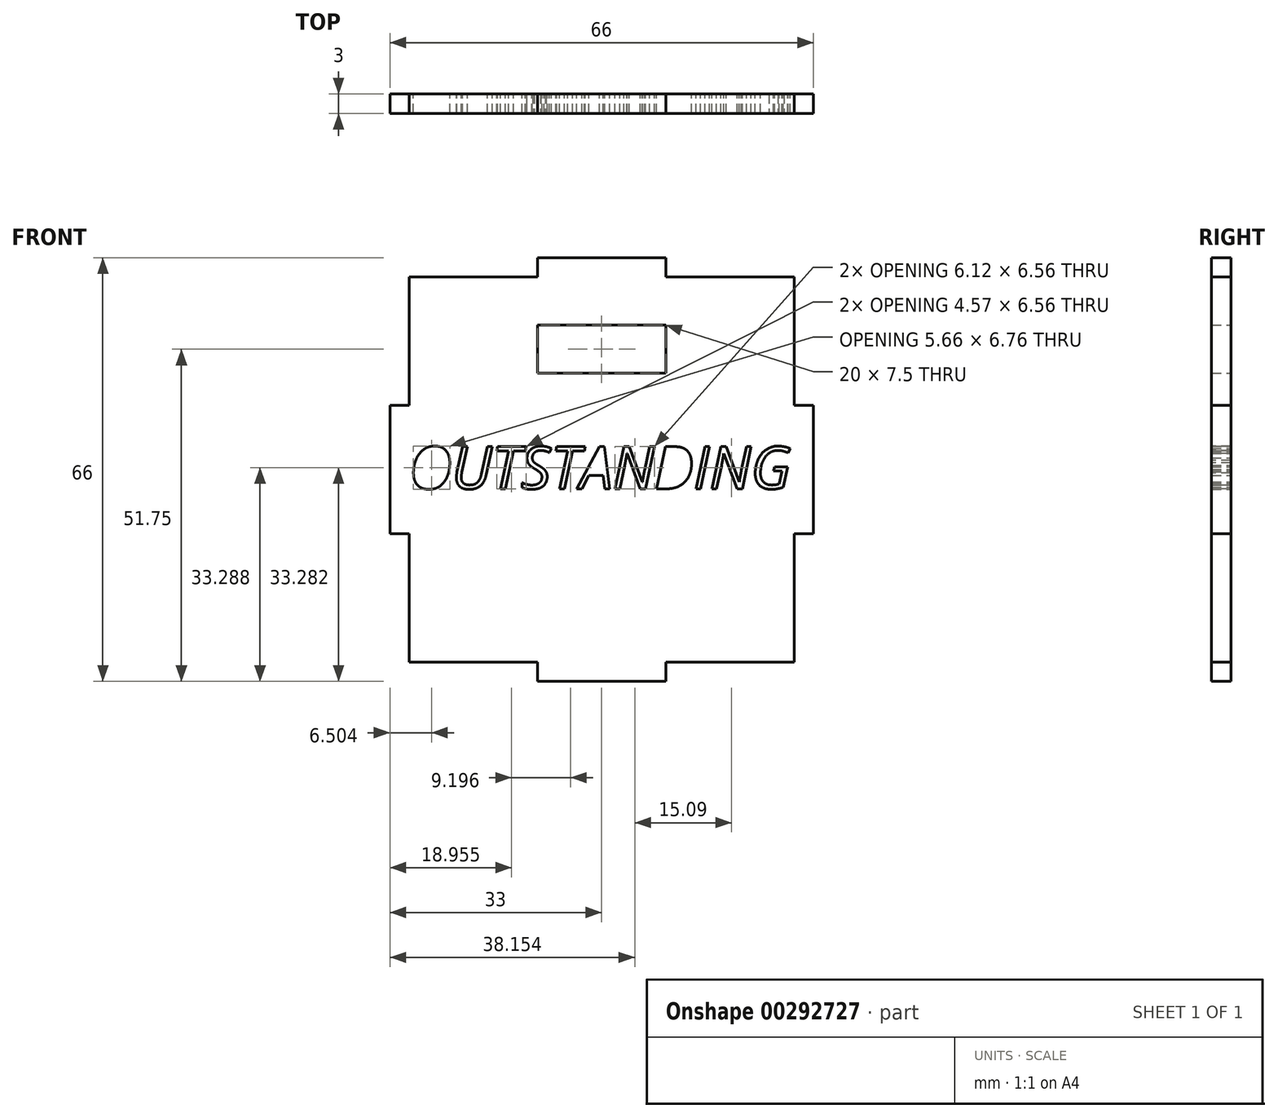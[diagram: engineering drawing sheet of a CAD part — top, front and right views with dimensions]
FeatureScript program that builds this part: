
annotation { "Feature Type Name" : "Feature", "Feature Type Description" : "" }
export const myFeature = defineFeature(function(context is Context, id is Id, definition is map)
    precondition{}
    {
        {
            var Q0;
            Q0=qCreatedBy(makeId("Front.planeOp"),FACE);
            var sketch = newSketch(context, id + "F0", { "sketchPlane" : qUnion([Q0])});
            skLineSegment(sketch, "E0", {"start": v(-33, 0) * mm, "end": v(-33, 10) * mm});
            skLineSegment(sketch, "E1", {"start": v(-33, 10) * mm, "end": v(-30, 10) * mm});
            skLineSegment(sketch, "E2", {"start": v(-30, 10) * mm, "end": v(-30, 30) * mm});
            skLineSegment(sketch, "E3", {"start": v(-30, 30) * mm, "end": v(-10, 30) * mm});
            skLineSegment(sketch, "E4", {"start": v(-10, 30) * mm, "end": v(-10, 33) * mm});
            skLineSegment(sketch, "E5", {"start": v(-10, 33) * mm, "end": v(0, 33) * mm});
            skLineSegment(sketch, "E6", {"start": v(-33, 0) * mm, "end": v(0, 0) * mm, "construction": true});
            skLineSegment(sketch, "E7", {"start": v(0, 0) * mm, "end": v(0, 33) * mm, "construction": true});
            skLineSegment(sketch, "E8.MirrorCS", {"start": v(33, 10) * mm, "end": v(30, 10) * mm});
            skLineSegment(sketch, "E9.MirrorCS", {"start": v(30, 10) * mm, "end": v(30, 30) * mm});
            skLineSegment(sketch, "E10.MirrorCS", {"start": v(30, 30) * mm, "end": v(10, 30) * mm});
            skLineSegment(sketch, "E11.MirrorCS", {"start": v(10, 30) * mm, "end": v(10, 33) * mm});
            skLineSegment(sketch, "E12.MirrorCS", {"start": v(33, 0) * mm, "end": v(33, 10) * mm});
            skLineSegment(sketch, "E13.MirrorCS", {"start": v(10, 33) * mm, "end": v(0, 33) * mm});
            skLineSegment(sketch, "E14.MirrorCS", {"start": v(33, -10) * mm, "end": v(30, -10) * mm});
            skLineSegment(sketch, "E15.MirrorCS", {"start": v(-10, -33) * mm, "end": v(0, -33) * mm});
            skLineSegment(sketch, "E16.MirrorCS", {"start": v(-33, 0) * mm, "end": v(-33, -10) * mm});
            skLineSegment(sketch, "E17.MirrorCS", {"start": v(30, -30) * mm, "end": v(10, -30) * mm});
            skLineSegment(sketch, "E18.MirrorCS", {"start": v(-33, -10) * mm, "end": v(-30, -10) * mm});
            skLineSegment(sketch, "E19.MirrorCS", {"start": v(-30, -10) * mm, "end": v(-30, -30) * mm});
            skLineSegment(sketch, "E20.MirrorCS", {"start": v(30, -10) * mm, "end": v(30, -30) * mm});
            skLineSegment(sketch, "E21.MirrorCS", {"start": v(10, -30) * mm, "end": v(10, -33) * mm});
            skLineSegment(sketch, "E22.MirrorCS", {"start": v(10, -33) * mm, "end": v(0, -33) * mm});
            skLineSegment(sketch, "E23.MirrorCS", {"start": v(-10, -30) * mm, "end": v(-10, -33) * mm});
            skLineSegment(sketch, "E24.MirrorCS", {"start": v(33, 0) * mm, "end": v(33, -10) * mm});
            skLineSegment(sketch, "E25.MirrorCS", {"start": v(-30, -30) * mm, "end": v(-10, -30) * mm});
            skLineSegment(sketch, "E26.bottom", {"start": v(10, 15) * mm, "end": v(-10, 15) * mm});
            skLineSegment(sketch, "E26.top", {"start": v(10, 22.5) * mm, "end": v(-10, 22.5) * mm});
            skLineSegment(sketch, "E26.left", {"start": v(10, 15) * mm, "end": v(10, 22.5) * mm});
            skLineSegment(sketch, "E26.right", {"start": v(-10, 15) * mm, "end": v(-10, 22.5) * mm});
            skPoint(sketch, "E26.middle", {"position": v(0, 18.75) * mm});
            skText(sketch, "E27", { "text": "OUTSTANDING", "fontName": "OpenSans-Italic.ttf"});
            const initialGuessF0  = {"E27": [-0.03, -0.003, 1, 0, 0.00662]};
            skSetInitialGuess(sketch, initialGuessF0);
            skSolve(sketch);
        }
        {
            var Q0;
            Q0 = qSketchRegion(id + "F0", true);
            extrude(context, id + "F1", {"entities" : qUnion([Q0]), "depth" : 3 * mm});
        }
    });
